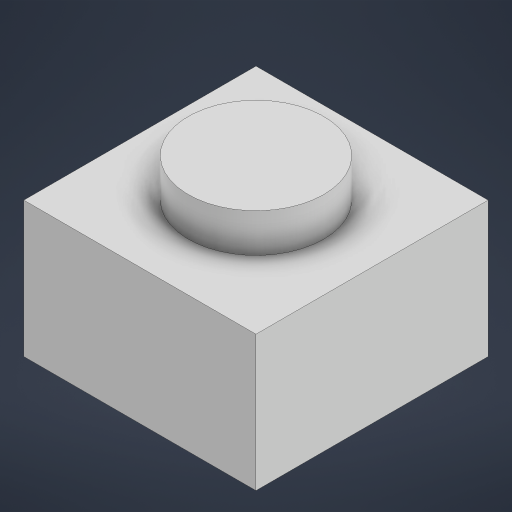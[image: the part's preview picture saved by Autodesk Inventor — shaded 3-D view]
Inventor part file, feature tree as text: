
AUTODESK INVENTOR PART (.ipt)
format: ipt  version: 2023 (Build 270158000, 158)  size: 159,232 bytes
history: native  units: in
note: dims shown in document units (in); Inventor stores cm internally (conversion verified against a paired STEP export)
features: extrude x2, sketch x2
ambient origin geometry x8: Origin, YZ Plane, XZ Plane, XY Plane, X Axis, Y Axis, Z Axis, Center Point
bodies: Solid1 (feature_tree)
feature tree (4):
  extrude  "Extrusion1"  Depth=0.2362in
  extrude  "Extrusion2"  Depth=0.1378in
  sketch  "Sketch1"  dims[d0=0.2362in d1=0.2362in]
  sketch  "Sketch2"  dims[d2=0.1378in d3=0.0in d4=0.1378in d5=0.0394in d6=0.0in]
